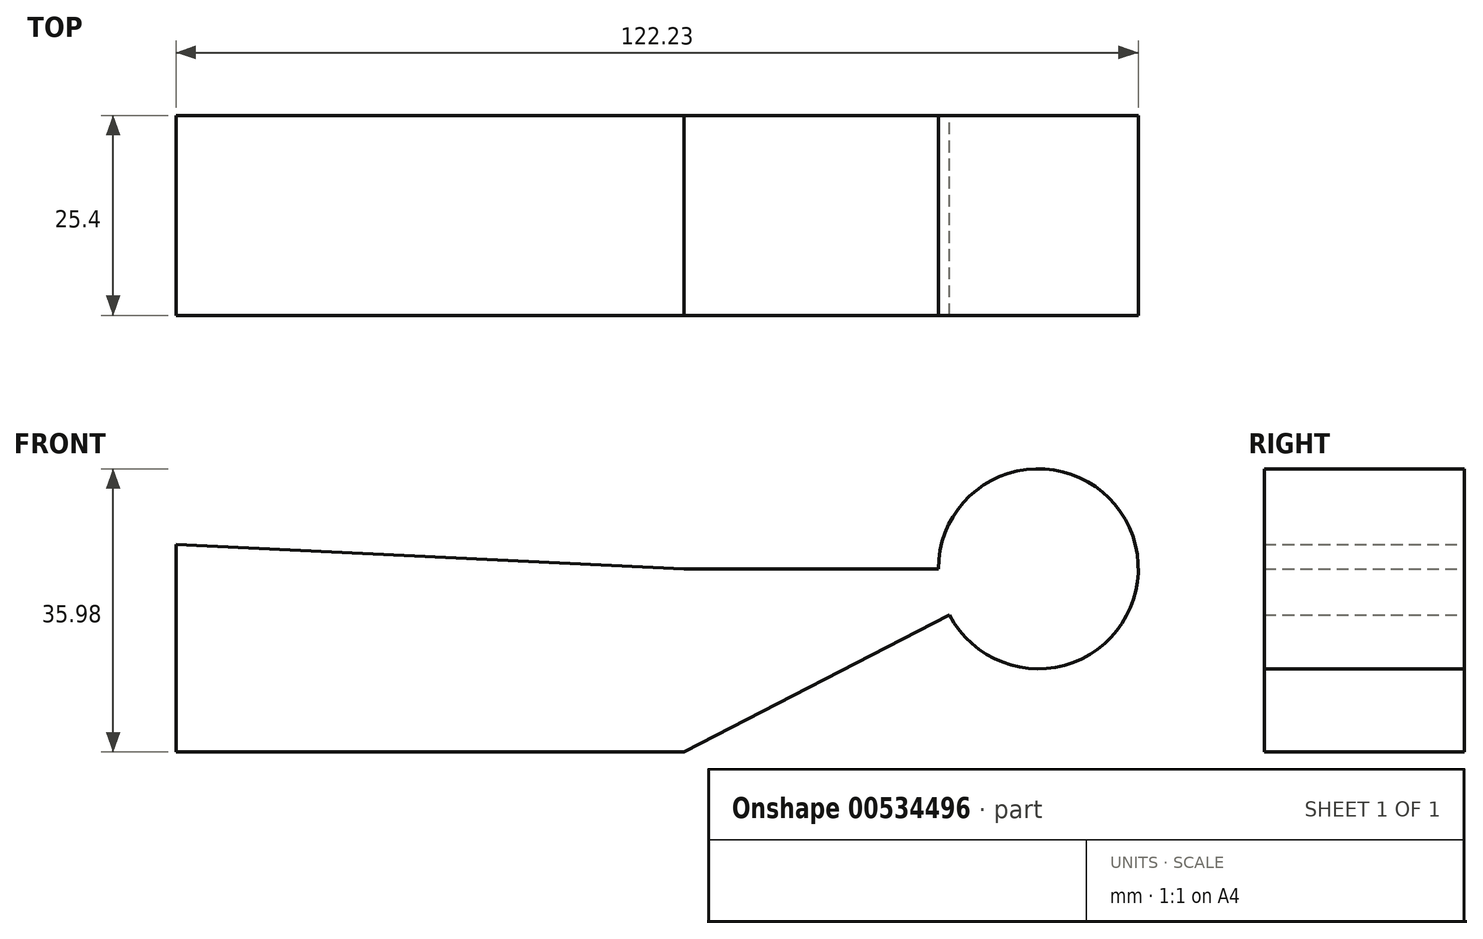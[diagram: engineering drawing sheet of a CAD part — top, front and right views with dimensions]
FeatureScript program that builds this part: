
annotation { "Feature Type Name" : "Feature", "Feature Type Description" : "" }
export const myFeature = defineFeature(function(context is Context, id is Id, definition is map)
    precondition{}
    {
        {
            var Q0;
            Q0=qCreatedBy(makeId("Front.planeOp"),FACE);
            var sketch = newSketch(context, id + "F0", { "sketchPlane" : qUnion([Q0])});
            skLineSegment(sketch, "E0", {"start": v(-82.9, 0.89) * mm, "end": v(-18.38, 0.89) * mm});
            skLineSegment(sketch, "E1", {"start": v(-18.38, 0.89) * mm, "end": v(-18.38, 24.17) * mm});
            skLineSegment(sketch, "E2", {"start": v(-18.38, 24.17) * mm, "end": v(26.63, 24.17) * mm});
            skCircle(sketch, "E3", {"center": v(26.63, 24.17) * mm, "radius": 12.7 * mm});
            skLineSegment(sketch, "E4", {"start": v(-82.9, 0.89) * mm, "end": v(-82.9, 27.27) * mm});
            skLineSegment(sketch, "E5", {"start": v(-82.9, 27.27) * mm, "end": v(-18.38, 24.17) * mm});
            skLineSegment(sketch, "E6", {"start": v(-18.38, 0.89) * mm, "end": v(26.63, 24.17) * mm});
            skSolve(sketch);
        }
        {
            var Q0;
            Q0 = qSketchRegion(id + "F0", true);
            extrude(context, id + "F1", {"entities" : qUnion([Q0]), "depth" : 25.4 * mm, "offsetDistance" : 25.4 * mm});
        }
    });
